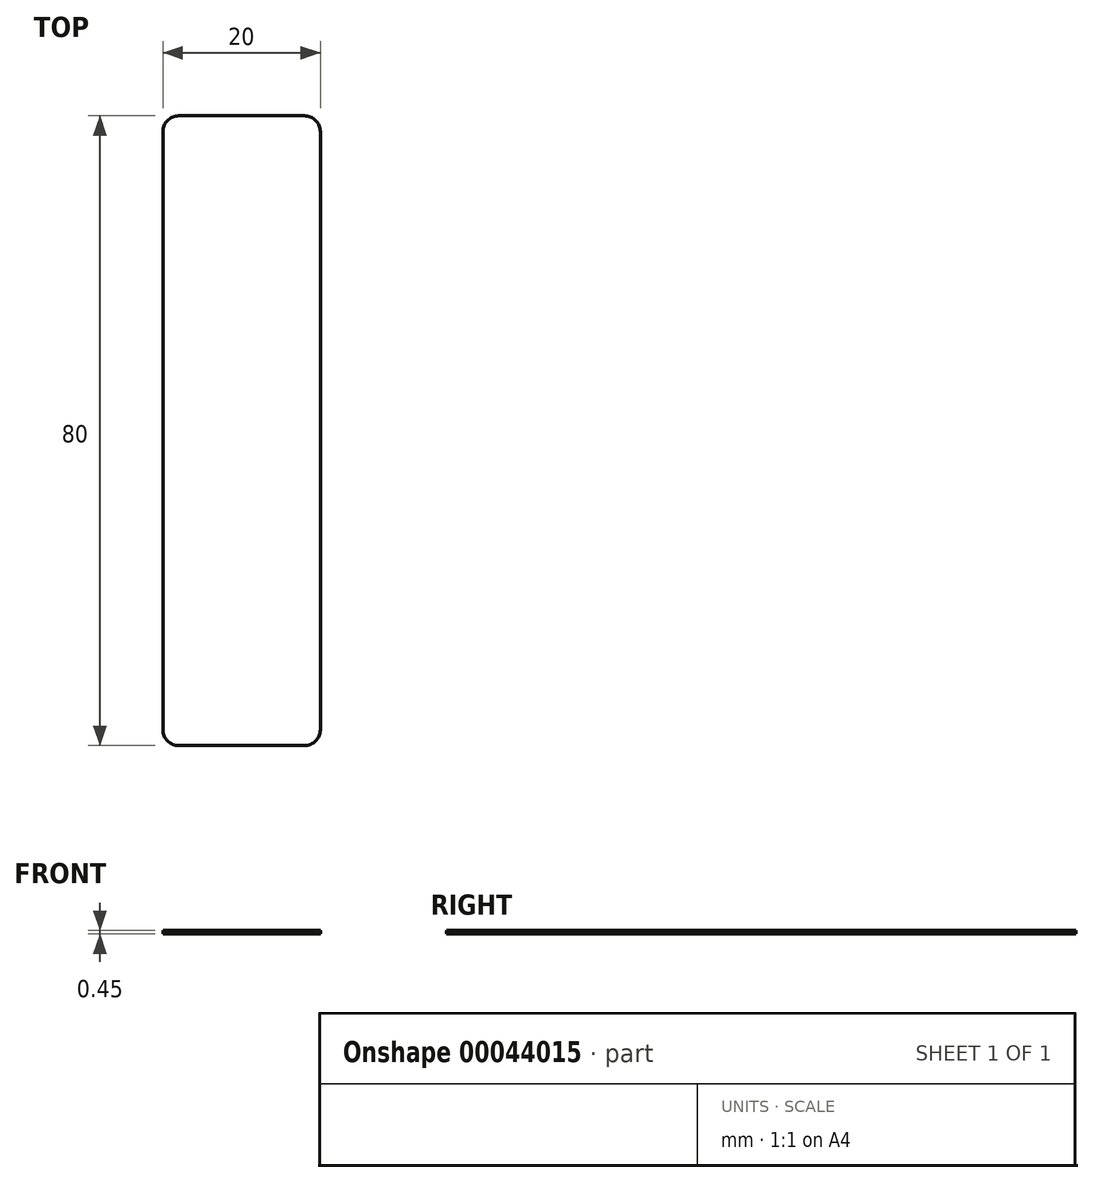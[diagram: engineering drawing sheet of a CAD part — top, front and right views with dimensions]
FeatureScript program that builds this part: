
annotation { "Feature Type Name" : "Feature", "Feature Type Description" : "" }
export const myFeature = defineFeature(function(context is Context, id is Id, definition is map)
    precondition{}
    {
        {
            var Q0;
            Q0=qCreatedBy(makeId("Top.planeOp"),FACE);
            var sketch = newSketch(context, id + "F0", { "sketchPlane" : qUnion([Q0])});
            skLineSegment(sketch, "E0.rect.bottom", {"start": v(10, -40) * mm, "end": v(-10, -40) * mm});
            skLineSegment(sketch, "E0.rect.top", {"start": v(10, 40) * mm, "end": v(-10, 40) * mm});
            skLineSegment(sketch, "E0.rect.left", {"start": v(10, -40) * mm, "end": v(10, 40) * mm});
            skLineSegment(sketch, "E0.rect.right", {"start": v(-10, -40) * mm, "end": v(-10, 40) * mm});
            skPoint(sketch, "E0.rect.middle", {"position": v(0, 0) * mm});
            skSolve(sketch);
        }
        {
            var Q0;
            Q0=makeQuery(id+"F0.imprint","IMPRINT",FACE,{"disambiguationData":[TD([[makeQuery(id+"F0.imprint","IMPRINT",EDGE,{"derivedFrom":sQuery(id+"F0.wireOp",EDGE,"E0.rect.bottom")}),-1.0]])]});
            extrude(context, id + "F1", {"entities" : qUnion([Q0]), "depth" : 0.45 * mm});
        }
        {
            var Q0;
            Q0=makeQuery(id+"F1.opExtrude","SWEPT_EDGE",EDGE,{"disambiguationData":[OSD([sQuery(id+"F0.wireOp",EDGE,"E0.rect.bottom"),sQuery(id+"F0.wireOp",EDGE,"E0.rect.right")])]});
            var Q1;
            Q1=makeQuery(id+"F1.opExtrude","SWEPT_EDGE",EDGE,{"disambiguationData":[OSD([sQuery(id+"F0.wireOp",EDGE,"E0.rect.bottom"),sQuery(id+"F0.wireOp",EDGE,"E0.rect.left")])]});
            var Q2;
            Q2=makeQuery(id+"F1.opExtrude","SWEPT_EDGE",EDGE,{"disambiguationData":[OSD([sQuery(id+"F0.wireOp",EDGE,"E0.rect.top"),sQuery(id+"F0.wireOp",EDGE,"E0.rect.left")])]});
            var Q3;
            Q3=makeQuery(id+"F1.opExtrude","SWEPT_EDGE",EDGE,{"disambiguationData":[OSD([sQuery(id+"F0.wireOp",EDGE,"E0.rect.top"),sQuery(id+"F0.wireOp",EDGE,"E0.rect.right")])]});
            fillet(context, id + "F2", {"entities" : qUnion([Q0, Q1, Q2, Q3]), "radius" : 2 * mm, "tangentPropagation" : true, "allowEdgeOverflow" : false});
        }
    });
